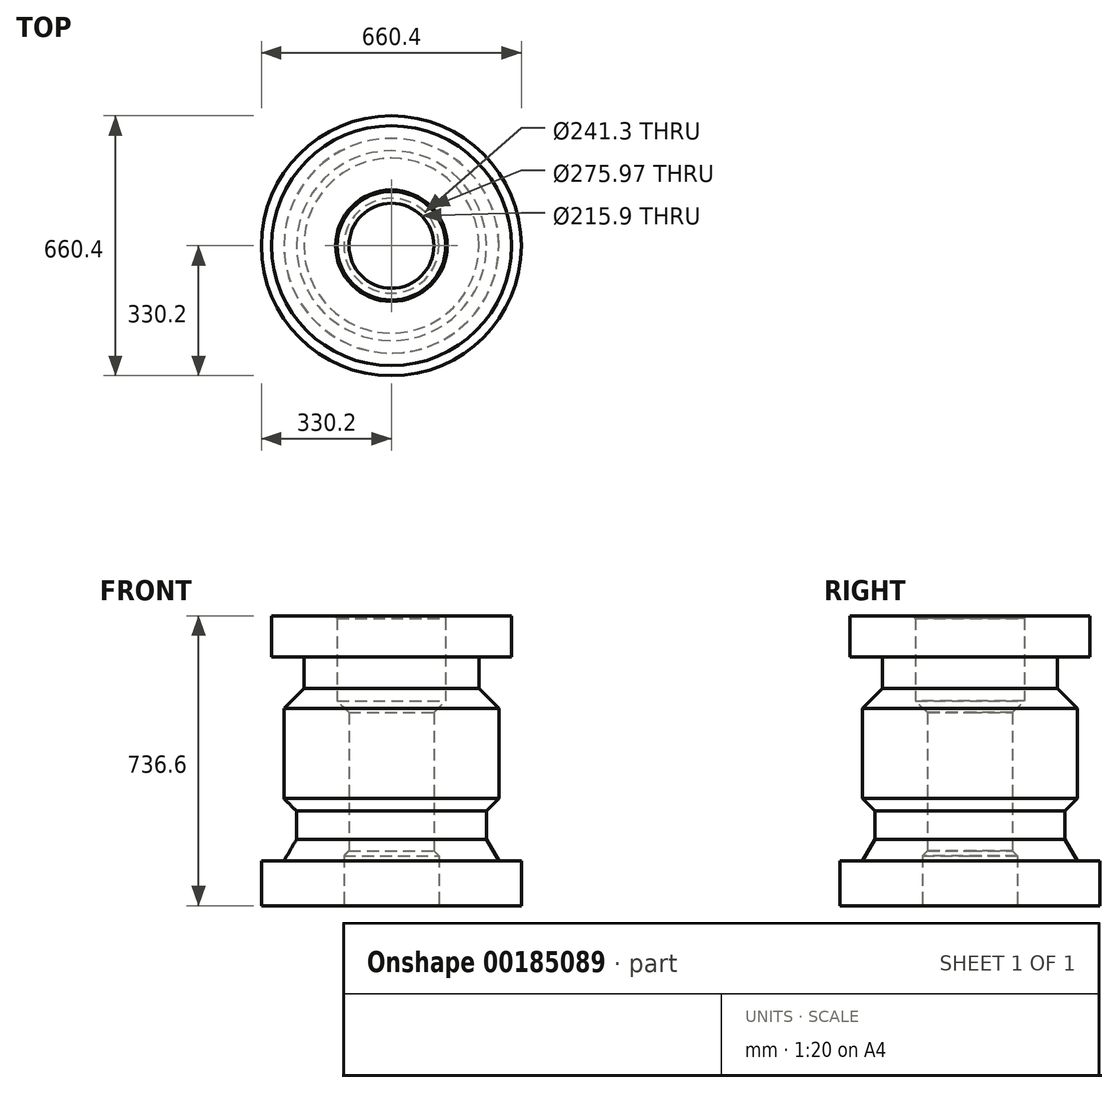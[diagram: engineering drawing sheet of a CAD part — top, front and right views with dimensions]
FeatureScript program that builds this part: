
annotation { "Feature Type Name" : "Feature", "Feature Type Description" : "" }
export const myFeature = defineFeature(function(context is Context, id is Id, definition is map)
    precondition{}
    {
        {
            var Q0;
            Q0=qCreatedBy(makeId("Front.planeOp"),FACE);
            var sketch = newSketch(context, id + "F0", { "sketchPlane" : qUnion([Q0])});
            skLineSegment(sketch, "E0", {"start": v(0, 0) * mm, "end": v(0, 516.78) * mm, "construction": true});
            skLineSegment(sketch, "E1", {"start": v(120.65, 0) * mm, "end": v(330.2, 0) * mm});
            skLineSegment(sketch, "E2", {"start": v(330.2, 0) * mm, "end": v(330.2, 114.3) * mm});
            skLineSegment(sketch, "E3", {"start": v(330.2, 114.3) * mm, "end": v(272.74, 114.3) * mm});
            skLineSegment(sketch, "E4", {"start": v(272.74, 114.3) * mm, "end": v(241.3, 168.76) * mm});
            skLineSegment(sketch, "E5", {"start": v(241.3, 168.76) * mm, "end": v(241.3, 240.34) * mm});
            skLineSegment(sketch, "E6", {"start": v(241.3, 240.34) * mm, "end": v(273.05, 272.09) * mm});
            skLineSegment(sketch, "E7", {"start": v(273.05, 272.09) * mm, "end": v(273.05, 500.92) * mm});
            skLineSegment(sketch, "E8", {"start": v(273.05, 500.92) * mm, "end": v(222.25, 551.72) * mm});
            skLineSegment(sketch, "E9", {"start": v(222.25, 551.72) * mm, "end": v(222.25, 632.46) * mm});
            skLineSegment(sketch, "E10", {"start": v(222.25, 632.46) * mm, "end": v(304.8, 632.46) * mm});
            skLineSegment(sketch, "E11", {"start": v(304.8, 632.46) * mm, "end": v(304.8, 736.6) * mm});
            skLineSegment(sketch, "E12", {"start": v(304.8, 736.6) * mm, "end": v(141.65, 736.6) * mm});
            skLineSegment(sketch, "E13", {"start": v(141.65, 736.6) * mm, "end": v(137.99, 730.25) * mm});
            skLineSegment(sketch, "E14", {"start": v(137.99, 730.25) * mm, "end": v(137.99, 520.7) * mm});
            skLineSegment(sketch, "E15", {"start": v(137.99, 520.7) * mm, "end": v(107.95, 490.66) * mm});
            skLineSegment(sketch, "E16", {"start": v(107.95, 490.66) * mm, "end": v(107.95, 139.7) * mm});
            skLineSegment(sketch, "E17", {"start": v(107.95, 139.7) * mm, "end": v(120.65, 127) * mm});
            skLineSegment(sketch, "E18", {"start": v(120.65, 127) * mm, "end": v(120.65, 0) * mm});
            skSolve(sketch);
        }
        {
            var Q0;
            Q0=makeQuery(id+"F0.imprint","IMPRINT",FACE,{"disambiguationData":[TD([[makeQuery(id+"F0.imprint","IMPRINT",EDGE,{"derivedFrom":sQuery(id+"F0.wireOp",EDGE,"E1")}),1.0]])]});
            var Q1;
            Q1=sQuery(id+"F0.wireOp",EDGE,"E0");
            revolve(context, id + "F1", {"entities" : qUnion([Q0]), "axis" : qUnion([Q1]), "revolveType" : RevolveType.FULL});
        }
    });
